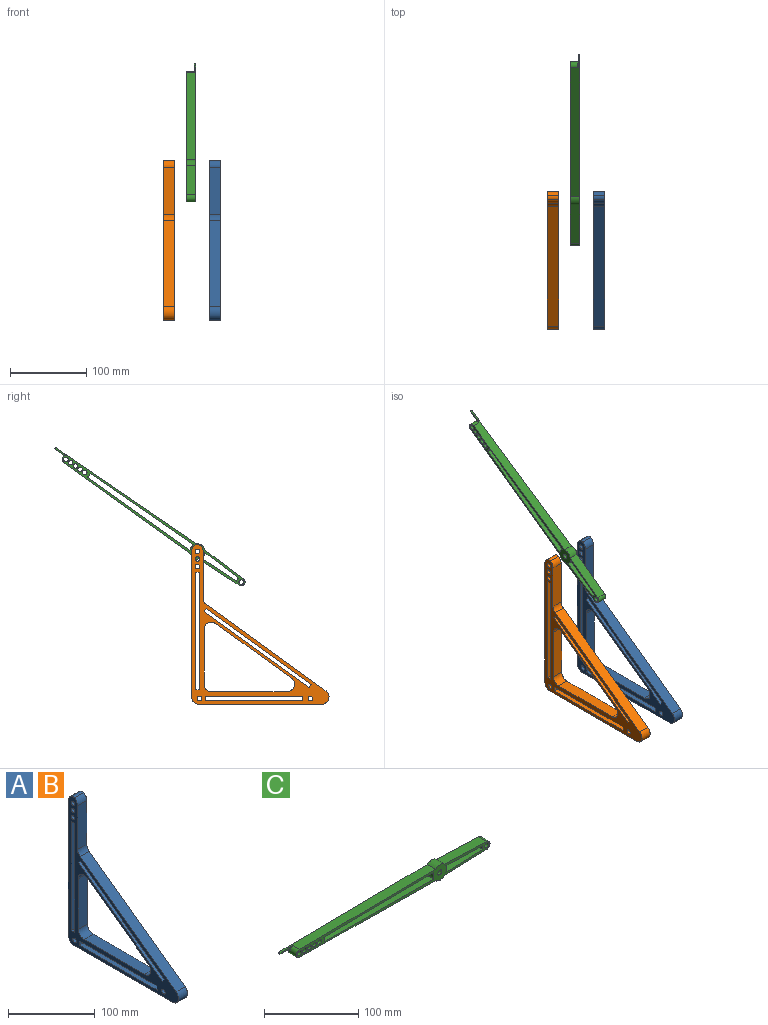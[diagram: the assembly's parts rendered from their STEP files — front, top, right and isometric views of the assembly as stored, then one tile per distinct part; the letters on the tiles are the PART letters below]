
ASSEMBLY  parts=3 mates=1
PART A: 35 faces, bbox 15x179.8x209.5 mm
  f0: plane 99.09x71.57mm, normal (0,0.59,-0.81), area 1833.5mm2, adj f24,f25,f31,f33
  f1: plane 71.57x15mm, normal (0,-1,0), area 1073.5mm2, adj f24,f25,f31,f32
  f2: plane 15x5mm, normal (0,0,-1), area 75mm2, adj f3,f14,f24,f25
  f3: plane 153.9x15mm, normal (0,-1,0), area 2308.4mm2, adj f2,f4,f24,f25
  f4: plane 15x5mm, normal (0,0,1), area 75mm2, adj f3,f14,f24,f25
  f5: plane 137.64x99.41mm, normal (0,0.59,-0.81), area 2546.8mm2, adj f6,f15,f24,f25
  f6: plane 15x4.05mm, normal (0,-0.81,-0.59), area 75mm2, adj f5,f7,f24,f25
  f7: plane 137.64x99.41mm, normal (0,-0.59,0.81), area 2546.8mm2, adj f6,f15,f24,f25
  f8: plane 15x6mm, normal (0,1,0), area 90mm2, adj f9,f16,f24,f25
  f9: plane 127x15mm, normal (0,0,-1), area 1904.9mm2, adj f8,f10,f24,f25
  f10: plane 15x6mm, normal (0,-1,0), area 90mm2, adj f9,f16,f24,f25
  f11: plane 61.79x15mm, normal (0,-1,0), area 926.9mm2, adj f24,f25,f27,f28
  f12: plane 156.79x113.23mm, normal (0,-0.59,0.81), area 2901mm2, adj f24,f25,f28,f29
  f13: plane 160.48x15mm, normal (0,0,-1), area 2407.2mm2, adj f24,f25,f29,f30
  f14: plane 153.9x15mm, normal (0,1,0), area 2308.4mm2, adj f2,f4,f24,f25
  f15: plane 15x4.05mm, normal (0,0.81,0.59), area 75mm2, adj f5,f7,f24,f25
  f16: plane 127x15mm, normal (0,0,1), area 1904.9mm2, adj f8,f10,f24,f25
  f17: cylinder r=3mm len=15mm, axis (-1,0,0), area 282.7mm2, adj f24,f25
  f18: plane 190.69x15mm, normal (0,1,0), area 2860.3mm2, adj f24,f25,f26,f30
  f19: cylinder r=3mm len=15mm, axis (-1,0,0), area 282.7mm2, adj f24,f25
  f20: cylinder r=3mm len=15mm, axis (-1,0,0), area 282.7mm2, adj f24,f25
  f21: cylinder r=3mm len=15mm, axis (-1,0,0), area 282.7mm2, adj f24,f25
  f22: cylinder r=3mm len=15mm, axis (-1,0,0), area 282.7mm2, adj f24,f25
  f23: plane 99.09x15mm, normal (0,0,1), area 1486.3mm2, adj f24,f25,f32,f33
  f24: plane 209.47x179.79mm, normal (1,0,0), area 6092.7mm2, adj f0,f1,f2,f3,f4,f5,f6,f7
  f25: plane 209.47x179.79mm, normal (-1,0,0), area 6092.7mm2, adj f0,f1,f2,f3,f4,f5,f6,f7
  f26: cylinder r=9.66mm len=15mm, axis (-1,0,0), area 157.8mm2, adj f18,f24,f25,f34
  f27: cylinder r=9.66mm len=15mm, axis (-1,0,0), area 157.8mm2, adj f11,f24,f25,f34
  f28: cylinder r=9.66mm len=15mm, axis (1,0,0), area 136.9mm2, adj f11,f12,f24,f25
  f29: cylinder r=9.66mm len=17.49mm, axis (1,0,0), area 364.5mm2, adj f12,f13,f24,f25
  f30: cylinder r=9.66mm len=15mm, axis (1,0,0), area 227.5mm2, adj f13,f18,f24,f25
  f31: cylinder r=9.66mm len=15.31mm, axis (1,0,0), area 318.1mm2, adj f0,f1,f24,f25
  f32: cylinder r=9.66mm len=15mm, axis (1,0,0), area 227.5mm2, adj f1,f23,f24,f25
  f33: cylinder r=9.66mm len=17.49mm, axis (1,0,0), area 364.5mm2, adj f0,f23,f24,f25
  f34: cylinder r=5mm len=15mm, axis (-1,0,0), area 72.2mm2, adj f24,f25,f26,f27
PART B: same geometry as A
PART C: 33 faces, bbox 305x12.5x20 mm
  f0: plane 63.12x12.5mm, normal (0.04,0,-1), area 789.5mm2, adj f3,f4,f7,f32
  f1: plane 203.3x12.5mm, normal (-0.01,0,1), area 2541.4mm2, adj f3,f4,f5,f11,f31
  f2: plane 63.12x12.5mm, normal (0.04,0,1), area 789.5mm2, adj f3,f4,f7,f31
  f3: plane 290x20mm, normal (0,-1,0), area 1875.8mm2, adj f0,f1,f2,f5,f6,f7,f8,f9
  f4: plane 305x20mm, normal (0,1,0), area 1914mm2, adj f0,f1,f2,f5,f6,f7,f8,f9
  f5: cylinder r=5mm len=12.5mm, axis (0,1,0), area 177.3mm2, adj f1,f3,f4,f6,f18,f19
  f6: plane 203.3x12.5mm, normal (-0.01,0,-1), area 2541.4mm2, adj f3,f4,f5,f32
  f7: cylinder r=5mm len=12.5mm, axis (0,1,0), area 196.3mm2, adj f0,f2,f3,f4
  f8: cylinder r=3mm len=12.5mm, axis (0,1,0), area 235.6mm2, adj f3,f4
  f9: cylinder r=3mm len=12.5mm, axis (0,1,0), area 235.6mm2, adj f3,f4
  f10: plane 13.32x2mm, normal (0,0,-1), area 26.6mm2, adj f4,f13,f15,f18
  f11: plane 19.05x3mm, normal (0,0,1), area 39.4mm2, adj f1,f4,f13,f14,f19
  f12: plane 2x0.34mm, normal (-1,0,0), area 0.7mm2, adj f4,f13,f14,f15
  f13: plane 16.68x2.3mm, normal (0,-1,0), area 34.2mm2, adj f10,f11,f12,f14,f15,f18,f19
  f14: cylinder r=0.95mm len=2mm, axis (0,1,0), area 3mm2, adj f4,f11,f12,f13
  f15: cylinder r=0.95mm len=2mm, axis (0,1,0), area 3mm2, adj f4,f10,f12,f13
  f16: cylinder r=3mm len=12.5mm, axis (0,-1,0), area 235.6mm2, adj f3,f4
  f17: cylinder r=3mm len=12.5mm, axis (0,-1,0), area 235.6mm2, adj f3,f4
  f18: cylinder r=1mm len=3mm, axis (0,1,0), area 4.3mm2, adj f4,f5,f10,f13,f19
  f19: torus R=6mm, axis (0,-1,0), area 7mm2, adj f5,f11,f13,f18
  f20: plane 164.57x12.5mm, normal (0.01,0,-1), area 2057.1mm2, adj f3,f4,f21,f23
  f21: cylinder r=6.85mm len=12.5mm, axis (0,-1,0), area 77.9mm2, adj f3,f4,f20,f22
  f22: plane 164.57x12.5mm, normal (0.01,0,1), area 2057.1mm2, adj f3,f4,f21,f23
  f23: cylinder r=10mm len=12.5mm, axis (0,-1,0), area 109.8mm2, adj f3,f4,f20,f22
  f24: cylinder r=3mm len=12.5mm, axis (0,-1,0), area 235.6mm2, adj f3,f4
  f25: cylinder r=3mm len=12.5mm, axis (0,-1,0), area 235.6mm2, adj f3,f4
  f26: cylinder r=3mm len=12.5mm, axis (0,-1,0), area 235.6mm2, adj f3,f4
  f27: cylinder r=6.28mm len=12.5mm, axis (0,-1,0), area 64.6mm2, adj f3,f4,f28,f30
  f28: plane 55.23x12.5mm, normal (-0.03,0,-1), area 690.7mm2, adj f3,f4,f27,f29
  f29: cylinder r=10mm len=12.5mm, axis (0,-1,0), area 109.8mm2, adj f3,f4,f28,f30
  f30: plane 55.23x12.5mm, normal (-0.03,0,1), area 690.7mm2, adj f3,f4,f27,f29
  f31: cylinder r=10mm len=13.58mm, axis (0,-1,0), area 186.7mm2, adj f1,f2,f3,f4
  f32: cylinder r=10mm len=13.59mm, axis (0,-1,0), area 186.7mm2, adj f0,f3,f4,f6
PLACE A t=(-97.64,98.23,-34.2)mm
PLACE B t=(-157.64,98.23,-34.2)mm
PLACE C rot(axis=(0.29,0.29,-0.91),95.2deg) t=(-115.14,90.73,165.8)mm
MATE revolute C.f8 <-> A.f21  axis (-1,0,0) through (-127.64,90.73,165.8)mm
